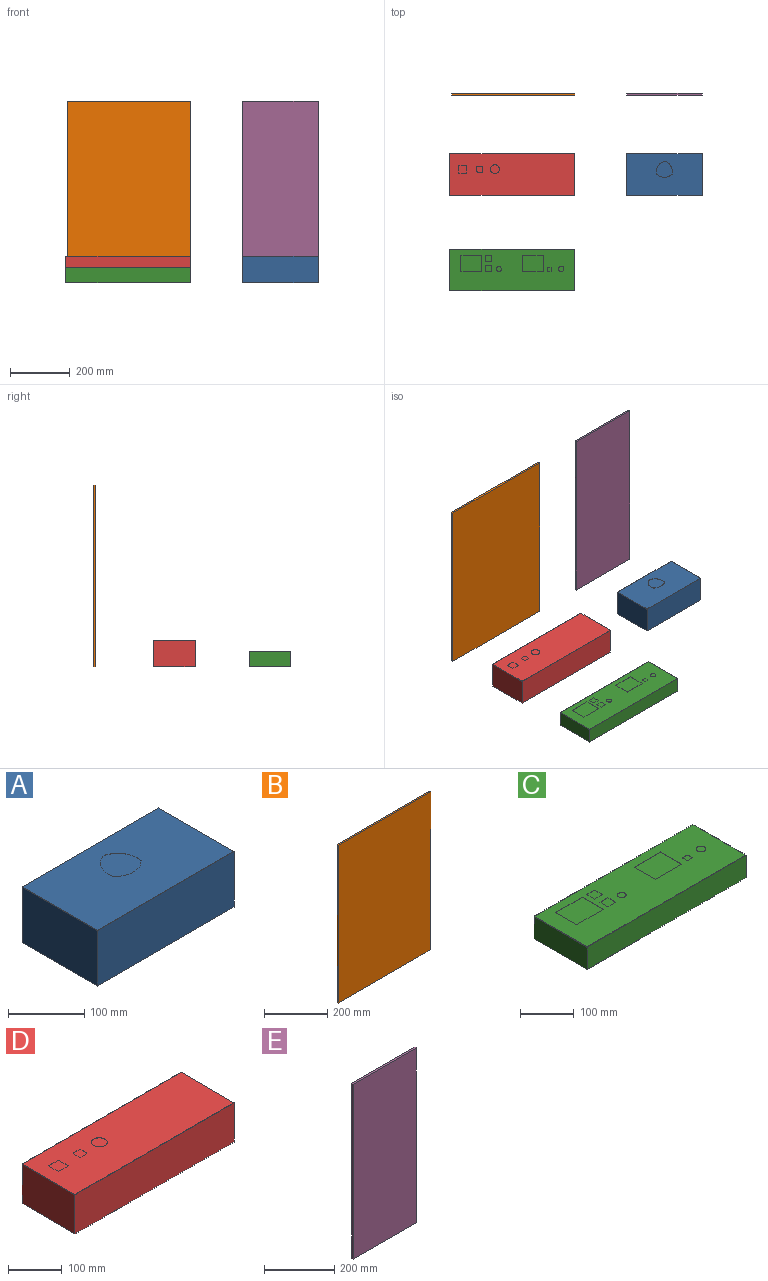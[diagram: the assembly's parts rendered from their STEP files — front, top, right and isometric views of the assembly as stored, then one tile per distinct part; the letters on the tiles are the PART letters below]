
ASSEMBLY  parts=5 mates=11
PART A: 17 faces, bbox 254x139.7x89.6 mm
  f0: plane 254x88.9mm, normal (0,1,0), area 22580.6mm2, adj f1,f7,f8,f9
  f1: plane 254x139.29mm, normal (0,0,1), area 35380.6mm2, adj f0,f2,f8,f9
  f2: plane 254x0.25mm, normal (0,1,0), area 64.5mm2, adj f1,f3,f8,f9
  f3: plane 254x139.29mm, normal (0,0,-1), area 33181.9mm2, adj f2,f4,f8,f9,f10,f11,f12,f13
  f4: plane 254x0.41mm, normal (0,1,0), area 103.2mm2, adj f3,f5,f8,f9
  f5: plane 254x139.7mm, normal (0,0,1), area 33285.2mm2, adj f4,f6,f8,f9,f10,f11,f12,f13
  f6: plane 254x89.56mm, normal (0,-1,0), area 22748.3mm2, adj f5,f7,f8,f9
  f7: plane 254x139.7mm, normal (0,0,-1), area 35483.8mm2, adj f0,f6,f8,f9
  f8: plane 139.7x89.56mm, normal (1,0,0), area 12476.2mm2, adj f0,f1,f2,f3,f4,f5,f6,f7
  f9: plane 139.7x89.56mm, normal (-1,0,0), area 12476.2mm2, adj f0,f1,f2,f3,f4,f5,f6,f7
  f10: extruded ~21.77x16mm, area 11.3mm2, adj f3,f5,f11,f14
  f11: extruded ~26.77x4.82mm, area 11.3mm2, adj f3,f5,f10,f12
  f12: extruded ~16.01x9.81mm, area 7.7mm2, adj f3,f5,f11,f13
  f13: extruded ~18.78x1.29mm, area 7.7mm2, adj f3,f5,f12,f15
  f14: extruded ~21.77x16mm, area 11.3mm2, adj f3,f5,f10,f16
  f15: extruded ~16.01x9.81mm, area 7.7mm2, adj f3,f5,f13,f16
  f16: extruded ~26.77x4.82mm, area 11.3mm2, adj f3,f5,f14,f15
PART B: 6 faces, bbox 412.8x6.4x609.6 mm
  f0: plane 609.6x6.35mm, normal (1,0,0), area 3871mm2, adj f1,f3,f4,f5
  f1: plane 412.75x6.35mm, normal (0,0,1), area 2621mm2, adj f0,f2,f4,f5
  f2: plane 609.6x6.35mm, normal (-1,0,0), area 3871mm2, adj f1,f3,f4,f5
  f3: plane 412.75x6.35mm, normal (0,0,-1), area 2621mm2, adj f0,f2,f4,f5
  f4: plane 609.6x412.75mm, normal (0,1,0), area 251612.4mm2, adj f0,f1,f2,f3
  f5: plane 609.6x412.75mm, normal (0,-1,0), area 251612.4mm2, adj f0,f1,f2,f3
PART C: 48 faces, bbox 419.1x139.7x51.5 mm
  f0: plane 419.1x50.8mm, normal (0,1,0), area 21290.3mm2, adj f1,f7,f8,f9
  f1: plane 419.1x139.29mm, normal (0,0,1), area 58377.9mm2, adj f0,f2,f8,f9
  f2: plane 419.1x0.25mm, normal (0,1,0), area 106.5mm2, adj f1,f3,f8,f9
  f3: plane 419.1x139.29mm, normal (0,0,-1), area 49107.3mm2, adj f2,f4,f8,f9,f10,f11,f12,f13
  f4: plane 419.1x0.41mm, normal (0,1,0), area 170.3mm2, adj f3,f5,f8,f9
  f5: plane 419.1x139.7mm, normal (0,0,1), area 49277.7mm2, adj f4,f6,f8,f9,f10,f11,f12,f13
  f6: plane 419.1x51.46mm, normal (0,-1,0), area 21567.1mm2, adj f5,f7,f8,f9
  f7: plane 419.1x139.7mm, normal (0,0,-1), area 58548.3mm2, adj f0,f6,f8,f9
  f8: plane 139.7x51.46mm, normal (1,0,0), area 7153.6mm2, adj f0,f1,f2,f3,f4,f5,f6,f7
  f9: plane 139.7x51.46mm, normal (-1,0,0), area 7153.6mm2, adj f0,f1,f2,f3,f4,f5,f6,f7
  f10: extruded ~1.68x0.7mm, area 0.8mm2, adj f3,f5,f11,f19
  f11: plane 8.73x0.41mm, normal (0,-1,0), area 3.5mm2, adj f3,f5,f10,f12
  f12: extruded ~1.68x0.7mm, area 0.8mm2, adj f3,f5,f11,f13
  f13: extruded ~1.68x0.7mm, area 0.8mm2, adj f3,f5,f12,f14
  f14: plane 8.73x0.41mm, normal (1,0,0), area 3.5mm2, adj f3,f5,f13,f15
  f15: extruded ~1.68x0.7mm, area 0.8mm2, adj f3,f5,f14,f16
  f16: extruded ~1.68x0.7mm, area 0.8mm2, adj f3,f5,f15,f17
  f17: plane 8.73x0.41mm, normal (0,1,0), area 3.5mm2, adj f3,f5,f16,f18
  f18: extruded ~1.68x0.7mm, area 0.8mm2, adj f3,f5,f17,f20
  f19: extruded ~1.68x0.7mm, area 0.8mm2, adj f3,f5,f10,f21
  f20: extruded ~1.68x0.7mm, area 0.8mm2, adj f3,f5,f18,f21
  f21: plane 8.73x0.41mm, normal (-1,0,0), area 3.5mm2, adj f3,f5,f19,f20
  f22: extruded ~6.45x2.67mm, area 2.9mm2, adj f3,f5,f23,f24
  f23: extruded ~6.45x2.67mm, area 2.9mm2, adj f3,f5,f22,f25
  f24: extruded ~12.91x2.67mm, area 5.8mm2, adj f3,f5,f22,f26
  f25: extruded ~12.91x2.67mm, area 5.8mm2, adj f3,f5,f23,f26
  f26: extruded ~12.91x2.67mm, area 5.8mm2, adj f3,f5,f24,f25
  f27: extruded ~5.89x2.44mm, area 2.7mm2, adj f3,f5,f28,f29
  f28: extruded ~5.89x2.44mm, area 2.7mm2, adj f3,f5,f27,f30
  f29: extruded ~11.79x2.44mm, area 5.3mm2, adj f3,f5,f27,f31
  f30: extruded ~11.79x2.44mm, area 5.3mm2, adj f3,f5,f28,f31
  f31: extruded ~11.79x2.44mm, area 5.3mm2, adj f3,f5,f29,f30
  f32: plane 55.56x0.41mm, normal (-1,0,0), area 22.6mm2, adj f3,f5,f33,f34
  f33: plane 69.85x0.41mm, normal (0,1,0), area 28.4mm2, adj f3,f5,f32,f35
  f34: plane 69.85x0.41mm, normal (0,-1,0), area 28.4mm2, adj f3,f5,f32,f35
  f35: plane 55.56x0.41mm, normal (1,0,0), area 22.6mm2, adj f3,f5,f33,f34
  f36: plane 20.64x0.41mm, normal (1,0,0), area 8.4mm2, adj f3,f5,f37,f38
  f37: plane 20.64x0.41mm, normal (0,-1,0), area 8.4mm2, adj f3,f5,f36,f39
  f38: plane 20.64x0.41mm, normal (0,1,0), area 8.4mm2, adj f3,f5,f36,f39
  f39: plane 20.64x0.41mm, normal (-1,0,0), area 8.4mm2, adj f3,f5,f37,f38
  f40: plane 20.64x0.41mm, normal (1,0,0), area 8.4mm2, adj f3,f5,f41,f42
  f41: plane 20.64x0.41mm, normal (0,-1,0), area 8.4mm2, adj f3,f5,f40,f43
  f42: plane 20.64x0.41mm, normal (0,1,0), area 8.4mm2, adj f3,f5,f40,f43
  f43: plane 20.64x0.41mm, normal (-1,0,0), area 8.4mm2, adj f3,f5,f41,f42
  f44: plane 69.85x0.41mm, normal (0,1,0), area 28.4mm2, adj f3,f5,f45,f46
  f45: plane 55.56x0.41mm, normal (1,0,0), area 22.6mm2, adj f3,f5,f44,f47
  f46: plane 55.56x0.41mm, normal (-1,0,0), area 22.6mm2, adj f3,f5,f44,f47
  f47: plane 69.85x0.41mm, normal (0,-1,0), area 28.4mm2, adj f3,f5,f45,f46
PART D: 29 faces, bbox 419.1x139.7x89.6 mm
  f0: plane 419.1x88.9mm, normal (0,1,0), area 37258mm2, adj f1,f7,f8,f9
  f1: plane 419.1x139.29mm, normal (0,0,1), area 58377.9mm2, adj f0,f2,f8,f9
  f2: plane 419.1x0.25mm, normal (0,1,0), area 106.5mm2, adj f1,f3,f8,f9
  f3: plane 419.1x139.29mm, normal (0,0,-1), area 56657mm2, adj f2,f4,f8,f9,f10,f11,f12,f13
  f4: plane 419.1x0.41mm, normal (0,1,0), area 170.3mm2, adj f3,f5,f8,f9
  f5: plane 419.1x139.7mm, normal (0,0,1), area 56827.5mm2, adj f4,f6,f8,f9,f10,f11,f12,f13
  f6: plane 419.1x89.56mm, normal (0,-1,0), area 37534.8mm2, adj f5,f7,f8,f9
  f7: plane 419.1x139.7mm, normal (0,0,-1), area 58548.3mm2, adj f0,f6,f8,f9
  f8: plane 139.7x89.56mm, normal (1,0,0), area 12476.2mm2, adj f0,f1,f2,f3,f4,f5,f6,f7
  f9: plane 139.7x89.56mm, normal (-1,0,0), area 12476.2mm2, adj f0,f1,f2,f3,f4,f5,f6,f7
  f10: extruded ~1.68x0.7mm, area 0.8mm2, adj f3,f5,f11,f19
  f11: plane 14.29x0.41mm, normal (0,-1,0), area 5.8mm2, adj f3,f5,f10,f12
  f12: extruded ~1.68x0.7mm, area 0.8mm2, adj f3,f5,f11,f13
  f13: extruded ~1.68x0.7mm, area 0.8mm2, adj f3,f5,f12,f14
  f14: plane 14.29x0.41mm, normal (1,0,0), area 5.8mm2, adj f3,f5,f13,f15
  f15: extruded ~1.68x0.7mm, area 0.8mm2, adj f3,f5,f14,f16
  f16: extruded ~1.68x0.7mm, area 0.8mm2, adj f3,f5,f15,f17
  f17: plane 14.29x0.41mm, normal (0,1,0), area 5.8mm2, adj f3,f5,f16,f18
  f18: extruded ~1.68x0.7mm, area 0.8mm2, adj f3,f5,f17,f20
  f19: extruded ~1.68x0.7mm, area 0.8mm2, adj f3,f5,f10,f21
  f20: extruded ~1.68x0.7mm, area 0.8mm2, adj f3,f5,f18,f21
  f21: plane 14.29x0.41mm, normal (-1,0,0), area 5.8mm2, adj f3,f5,f19,f20
  f22: plane 26.19x0.41mm, normal (0,1,0), area 10.6mm2, adj f3,f5,f23,f24
  f23: plane 26.19x0.41mm, normal (1,0,0), area 10.6mm2, adj f3,f5,f22,f25
  f24: plane 26.19x0.41mm, normal (-1,0,0), area 10.6mm2, adj f3,f5,f22,f25
  f25: plane 26.19x0.41mm, normal (0,-1,0), area 10.6mm2, adj f3,f5,f23,f24
  f26: extruded ~29.33x25.07mm, area 28.1mm2, adj f3,f5,f27,f28
  f27: extruded ~10.38x4.3mm, area 4.7mm2, adj f3,f5,f26,f28
  f28: extruded ~10.38x4.3mm, area 4.7mm2, adj f3,f5,f26,f27
PART E: 6 faces, bbox 254x6.4x609.6 mm
  f0: plane 609.6x6.35mm, normal (1,0,0), area 3871mm2, adj f1,f3,f4,f5
  f1: plane 254x6.35mm, normal (0,0,1), area 1612.9mm2, adj f0,f2,f4,f5
  f2: plane 609.6x6.35mm, normal (-1,0,0), area 3871mm2, adj f1,f3,f4,f5
  f3: plane 254x6.35mm, normal (0,0,-1), area 1612.9mm2, adj f0,f2,f4,f5
  f4: plane 609.6x254mm, normal (0,1,0), area 154838.4mm2, adj f0,f1,f2,f3
  f5: plane 609.6x254mm, normal (0,-1,0), area 154838.4mm2, adj f0,f1,f2,f3
PLACE A t=(326.52,-108.93,-77.43)mm
PLACE B t=(25.63,86.65,-77.43)mm fixed
PLACE C t=(-183.92,-429.35,-77.43)mm
PLACE D t=(-183.92,-108.93,-77.43)mm
PLACE E t=(453.52,86.65,-77.43)mm
MATE planar D.f8 <-> C.f8  axis (1,0,0) through (25.63,-108.93,-32.98)mm
MATE planar A.f7 <-> E.f3  axis (0,0,-1) through (326.52,-178.78,-77.43)mm
MATE planar A.f9 <-> E.f2  axis (-1,0,0) through (199.52,-178.78,-32.77)mm
MATE planar D.f7 <-> C.f7  axis (0,0,-1) through (-183.92,-178.78,-77.43)mm
MATE planar B.f3 <-> D.f7  axis (0,0,-1) through (-180.74,89.82,-77.43)mm
MATE planar D.f7 <-> A.f7  axis (0,0,-1) through (-183.92,-108.93,-77.43)mm
MATE parallel D.f0 <-> B.f5  axis (0,1,0) through (-183.92,-108.93,-32.98)mm
MATE planar B.f0 <-> D.f8  axis (1,0,0) through (25.63,89.82,227.37)mm
MATE parallel C.f0 <-> D.f6  axis (0,1,0) through (-183.92,-429.35,-52.03)mm
MATE planar B.f5 <-> E.f5  axis (0,-1,0) through (-180.74,86.65,227.37)mm
MATE parallel A.f0 <-> E.f5  axis (0,1,0) through (326.52,-108.93,-32.98)mm
